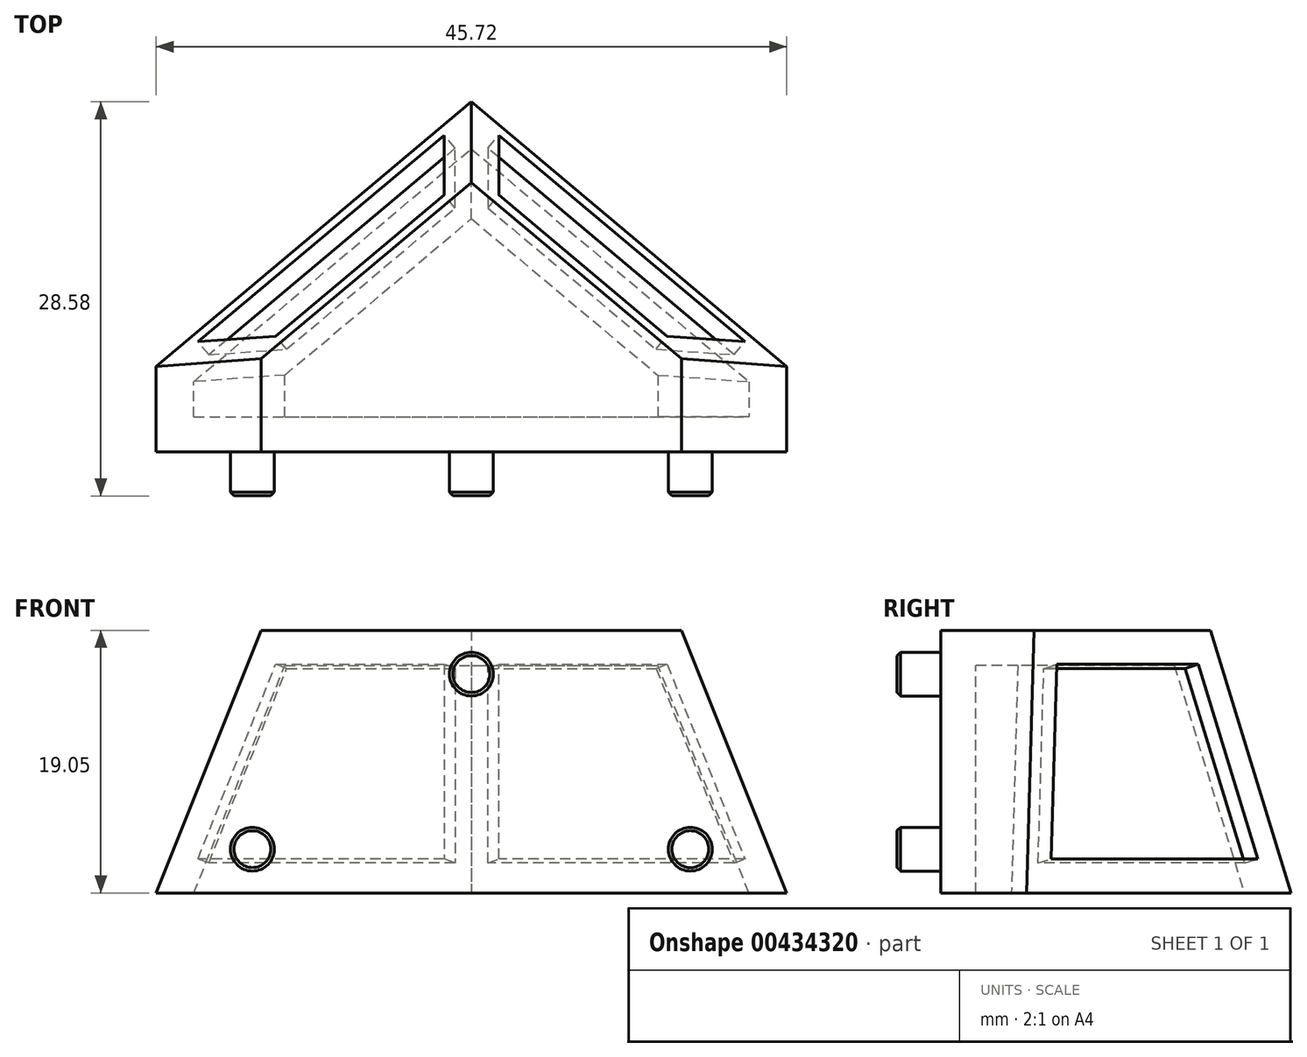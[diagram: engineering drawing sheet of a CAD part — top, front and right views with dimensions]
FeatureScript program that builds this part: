
annotation { "Feature Type Name" : "Feature", "Feature Type Description" : "" }
export const myFeature = defineFeature(function(context is Context, id is Id, definition is map)
    precondition{}
    {
        {
            var Q0;
            Q0=qCreatedBy(makeId("Top.planeOp"),FACE);
            var sketch = newSketch(context, id + "F0", { "sketchPlane" : qUnion([Q0])});
            skLineSegment(sketch, "E0", {"start": v(0, 0) * mm, "end": v(-22.86, 0) * mm});
            skLineSegment(sketch, "E1.MirrorCS", {"start": v(0, 0) * mm, "end": v(22.86, 0) * mm});
            skLineSegment(sketch, "E2", {"start": v(-22.86, 0) * mm, "end": v(-22.86, 6.22) * mm});
            skLineSegment(sketch, "E3", {"start": v(-22.86, 6.22) * mm, "end": v(0, 25.4) * mm});
            skLineSegment(sketch, "E4", {"start": v(0, 25.4) * mm, "end": v(22.86, 6.22) * mm});
            skLineSegment(sketch, "E5", {"start": v(22.86, 6.22) * mm, "end": v(22.86, 0) * mm});
            skSolve(sketch);
        }
        {
            var Q0;
            Q0=qCreatedBy(makeId("Top.planeOp"),FACE);
            cPlane(context, id + "F1", {"entities" : qUnion([Q0]), "cplaneType" : CPlaneType.OFFSET, "offset" : 19.05 * mm, "width" : 152.4 * mm, "height" : 152.4 * mm});
        }
        {
            var Q0;
            Q0=qCreatedBy(id+"F1.planeOp",FACE);
            var sketch = newSketch(context, id + "F2", { "sketchPlane" : qUnion([Q0])});
            skLineSegment(sketch, "E6", {"start": v(0, 0) * mm, "end": v(15.24, 0) * mm});
            skLineSegment(sketch, "E7.MirrorCS", {"start": v(0, 0) * mm, "end": v(-15.24, 0) * mm});
            skLineSegment(sketch, "E8", {"start": v(-15.24, 0) * mm, "end": v(-15.24, 6.76) * mm});
            skLineSegment(sketch, "E9", {"start": v(-15.24, 6.76) * mm, "end": v(0, 19.55) * mm});
            skLineSegment(sketch, "E10", {"start": v(0, 19.55) * mm, "end": v(15.24, 6.76) * mm});
            skLineSegment(sketch, "E11", {"start": v(15.24, 6.76) * mm, "end": v(15.24, 0) * mm});
            skSolve(sketch);
        }
        {
            var Q0;
            Q0=makeQuery(id+"F2.imprint","IMPRINT",FACE,{"disambiguationData":[TD([[makeQuery(id+"F2.imprint","IMPRINT",EDGE,{"derivedFrom":sQuery(id+"F2.wireOp",EDGE,"E6")}),1.0]])]});
            var Q1;
            Q1=makeQuery(id+"F0.imprint","IMPRINT",FACE,{"disambiguationData":[TD([[makeQuery(id+"F0.imprint","IMPRINT",EDGE,{"derivedFrom":sQuery(id+"F0.wireOp",EDGE,"E0")}),-1.0]])]});
            loft(context, id + "F3", {"sheetProfilesArray" : [{ "sheetProfileEntities" : qUnion([Q0]) }, { "sheetProfileEntities" : qUnion([Q1]) }]});
        }
        {
            var Q0;
            Q0=makeQuery(id+"F3.opLoft","CAP_FACE",FACE,{"disambiguationData":[OSD([makeQuery(id+"F0.imprint","IMPRINT",FACE,{"disambiguationData":[TD([[makeQuery(id+"F0.imprint","IMPRINT",EDGE,{"derivedFrom":sQuery(id+"F0.wireOp",EDGE,"E0")}),-1.0]])]})])],"isStart":true});
            shell(context, id + "F4", {"entities" : qUnion([Q0]), "thickness" : 2.54 * mm});
        }
        {
            var Q0;
            Q0=makeQuery(id+"F3.opLoft","SWEPT_FACE",FACE,{"disambiguationData":[OSD([sQuery(id+"F0.wireOp",EDGE,"E2"),sQuery(id+"F0.wireOp",EDGE,"E3"),sQuery(id+"F0.wireOp",EDGE,"E4"),sQuery(id+"F2.wireOp",EDGE,"E8"),sQuery(id+"F2.wireOp",EDGE,"E9"),sQuery(id+"F2.wireOp",EDGE,"E10")])]});
            var sketch = newSketch(context, id + "F5", { "sketchPlane" : qUnion([Q0])});
            skLineSegment(sketch, "E12.0", {"start": v(-12.65, 10.37) * mm, "end": v(-12.65, -4.38) * mm});
            skLineSegment(sketch, "E12.1", {"start": v(3, 13.38) * mm, "end": v(-12.65, 10.37) * mm});
            skLineSegment(sketch, "E12.2", {"start": v(10.23, 0.01) * mm, "end": v(3, 13.38) * mm});
            skLineSegment(sketch, "E12.3", {"start": v(-12.65, -4.38) * mm, "end": v(10.23, 0.01) * mm});
            skSolve(sketch);
        }
        {
            var Q0;
            Q0=makeQuery(id+"F5.imprint","IMPRINT",FACE,{"disambiguationData":[TD([[makeQuery(id+"F5.imprint","IMPRINT",EDGE,{"derivedFrom":sQuery(id+"F5.wireOp",EDGE,"E12.0")}),1.0]])]});
            extrude(context, id + "F6", {"entities" : qUnion([Q0]), "operationType" : NewBodyOperationType.REMOVE, "oppositeDirection" : true, "depth" : 1.27 * mm});
        }
        {
            var Q0;
            Q0=makeQuery(id+"F3.opLoft","SWEPT_FACE",FACE,{"disambiguationData":[OSD([sQuery(id+"F0.wireOp",EDGE,"E3"),sQuery(id+"F0.wireOp",EDGE,"E4"),sQuery(id+"F0.wireOp",EDGE,"E5"),sQuery(id+"F2.wireOp",EDGE,"E9"),sQuery(id+"F2.wireOp",EDGE,"E10"),sQuery(id+"F2.wireOp",EDGE,"E11")])]});
            var sketch = newSketch(context, id + "F7", { "sketchPlane" : qUnion([Q0])});
            skLineSegment(sketch, "E13.0", {"start": v(-3, 13.38) * mm, "end": v(-10.23, 0.01) * mm});
            skLineSegment(sketch, "E13.1", {"start": v(12.65, 10.37) * mm, "end": v(-3, 13.38) * mm});
            skLineSegment(sketch, "E13.2", {"start": v(12.65, -4.38) * mm, "end": v(12.65, 10.37) * mm});
            skLineSegment(sketch, "E13.3", {"start": v(-10.23, 0.01) * mm, "end": v(12.65, -4.38) * mm});
            skSolve(sketch);
        }
        {
            var Q0;
            Q0=makeQuery(id+"F7.imprint","IMPRINT",FACE,{"disambiguationData":[TD([[makeQuery(id+"F7.imprint","IMPRINT",EDGE,{"derivedFrom":sQuery(id+"F7.wireOp",EDGE,"E13.0")}),1.0]])]});
            extrude(context, id + "F8", {"entities" : qUnion([Q0]), "operationType" : NewBodyOperationType.REMOVE, "oppositeDirection" : true, "depth" : 1.27 * mm});
        }
        {
            var Q0;
            Q0=makeQuery(id+"F3.opLoft","SWEPT_FACE",FACE,{"disambiguationData":[OSD([sQuery(id+"F0.wireOp",EDGE,"E0"),sQuery(id+"F0.wireOp",EDGE,"E1.MirrorCS"),sQuery(id+"F0.wireOp",EDGE,"E5"),sQuery(id+"F2.wireOp",EDGE,"E6"),sQuery(id+"F2.wireOp",EDGE,"E7.MirrorCS"),sQuery(id+"F2.wireOp",EDGE,"E11")])]});
            var sketch = newSketch(context, id + "F9", { "sketchPlane" : qUnion([Q0])});
            skCircle(sketch, "E14", {"center": v(0, 15.88) * mm, "radius": 1.59 * mm});
            skCircle(sketch, "E15", {"center": v(15.88, 3.18) * mm, "radius": 1.59 * mm});
            skCircle(sketch, "E16", {"center": v(-15.88, 3.18) * mm, "radius": 1.59 * mm});
            skSolve(sketch);
        }
        {
            var Q0;
            Q0=makeQuery(id+"F9.imprint","IMPRINT",FACE,{"disambiguationData":[TD([[makeQuery(id+"F9.imprint","IMPRINT",EDGE,{"derivedFrom":sQuery(id+"F9.wireOp",EDGE,"E16")}),1.0]])]});
            var Q1;
            Q1=makeQuery(id+"F9.imprint","IMPRINT",FACE,{"disambiguationData":[TD([[makeQuery(id+"F9.imprint","IMPRINT",EDGE,{"derivedFrom":sQuery(id+"F9.wireOp",EDGE,"E14")}),1.0]])]});
            var Q2;
            Q2=makeQuery(id+"F9.imprint","IMPRINT",FACE,{"disambiguationData":[TD([[makeQuery(id+"F9.imprint","IMPRINT",EDGE,{"derivedFrom":sQuery(id+"F9.wireOp",EDGE,"E15")}),1.0]])]});
            extrude(context, id + "F10", {"entities" : qUnion([Q0, Q1, Q2]), "operationType" : NewBodyOperationType.ADD, "depth" : 2.92 * mm});
        }
        {
            var Q0;
            Q0=makeQuery(id+"F10.opExtrude","CAP_FACE",FACE,{"disambiguationData":[OSD([sQuery(id+"F9.wireOp",EDGE,"E14")])],"isStart":false});
            var sketch = newSketch(context, id + "F11", { "sketchPlane" : qUnion([Q0])});
            skCircle(sketch, "E17", {"center": v(0, 15.88) * mm, "radius": 1.59 * mm});
            skSolve(sketch);
        }
        {
            var Q0;
            Q0=qSketchRegion(id+"F11",true);
            extrude(context, id + "F12", {"entities" : qUnion([Q0]), "operationType" : NewBodyOperationType.ADD, "depth" : 0.25 * mm, "hasDraft" : true, "draftAngle" : 45 * degree, "draftPullDirection" : true});
        }
        {
            var Q0;
            Q0=makeQuery(id+"F10.opExtrude","CAP_FACE",FACE,{"disambiguationData":[OSD([sQuery(id+"F9.wireOp",EDGE,"E15")])],"isStart":false});
            var sketch = newSketch(context, id + "F13", { "sketchPlane" : qUnion([Q0])});
            skCircle(sketch, "E18", {"center": v(15.88, 3.18) * mm, "radius": 1.6 * mm});
            skSolve(sketch);
        }
        {
            var Q0;
            Q0=makeQuery(id+"F10.opExtrude","CAP_FACE",FACE,{"disambiguationData":[OSD([sQuery(id+"F9.wireOp",EDGE,"E16")])],"isStart":false});
            var sketch = newSketch(context, id + "F14", { "sketchPlane" : qUnion([Q0])});
            skCircle(sketch, "E19", {"center": v(-15.88, 3.18) * mm, "radius": 1.59 * mm});
            skSolve(sketch);
        }
        {
            var Q0;
            Q0=qSketchRegion(id+"F13",true);
            var Q1;
            Q1=qSketchRegion(id+"F14",true);
            extrude(context, id + "F15", {"entities" : qUnion([Q0, Q1]), "operationType" : NewBodyOperationType.ADD, "depth" : 0.25 * mm, "hasDraft" : true, "draftAngle" : 45 * degree, "draftPullDirection" : true});
        }
    });
